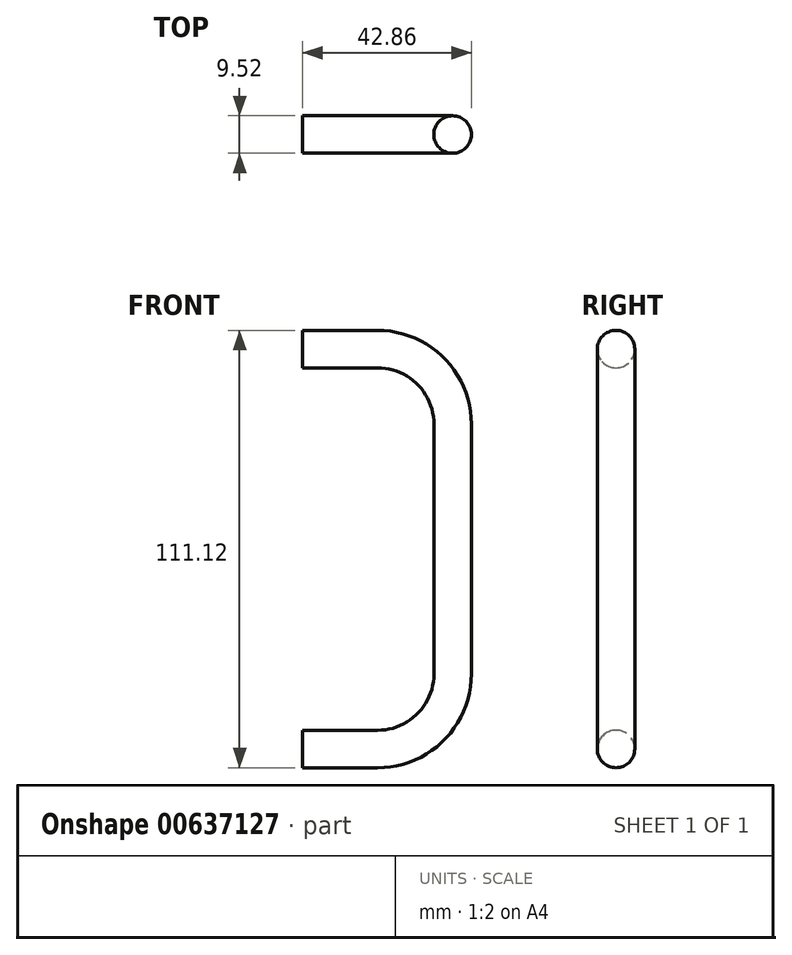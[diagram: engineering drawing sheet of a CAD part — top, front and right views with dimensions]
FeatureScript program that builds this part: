
annotation { "Feature Type Name" : "Feature", "Feature Type Description" : "" }
export const myFeature = defineFeature(function(context is Context, id is Id, definition is map)
    precondition{}
    {
        {
            var Q0;
            Q0=qCreatedBy(makeId("Right.planeOp"),FACE);
            var sketch = newSketch(context, id + "F0", { "sketchPlane" : qUnion([Q0])});
            skCircle(sketch, "E0", {"center": v(0, 0) * mm, "radius": 4.76 * mm});
            skSolve(sketch);
        }
        {
            var Q0;
            Q0=qCreatedBy(makeId("Front.planeOp"),FACE);
            var sketch = newSketch(context, id + "F1", { "sketchPlane" : qUnion([Q0])});
            skLineSegment(sketch, "E1", {"start": v(0, 0) * mm, "end": v(19.05, 0) * mm});
            skLineSegment(sketch, "E2", {"start": v(38.1, -19.05) * mm, "end": v(38.1, -82.55) * mm});
            skLineSegment(sketch, "E3", {"start": v(19.05, -101.6) * mm, "end": v(0, -101.6) * mm});
            skPoint(sketch, "E4.visualSharp", {"position": v(38.1, 0) * mm});
            skArc(sketch, "E4.filletArc", {"start": v(38.1, -19.05) * mm, "mid": v(32.52, -5.58) * mm, "end": v(19.05, 0) * mm});
            skPoint(sketch, "E5.visualSharp", {"position": v(38.1, -101.6) * mm});
            skArc(sketch, "E5.filletArc", {"start": v(19.05, -101.6) * mm, "mid": v(32.52, -96.02) * mm, "end": v(38.1, -82.55) * mm});
            skSolve(sketch);
        }
        {
            var Q0;
            Q0 = qSketchRegion(id + "F0", true);
            var Q1;
            Q1 = qConstructionFilter(qBodyType(qCreatedBy(id + "F1" ,EDGE), BodyType.WIRE), ConstructionObject.NO);
            sweep(context, id + "F2", {"profiles" : qUnion([Q0]), "path" : qUnion([Q1])});
        }
    });
